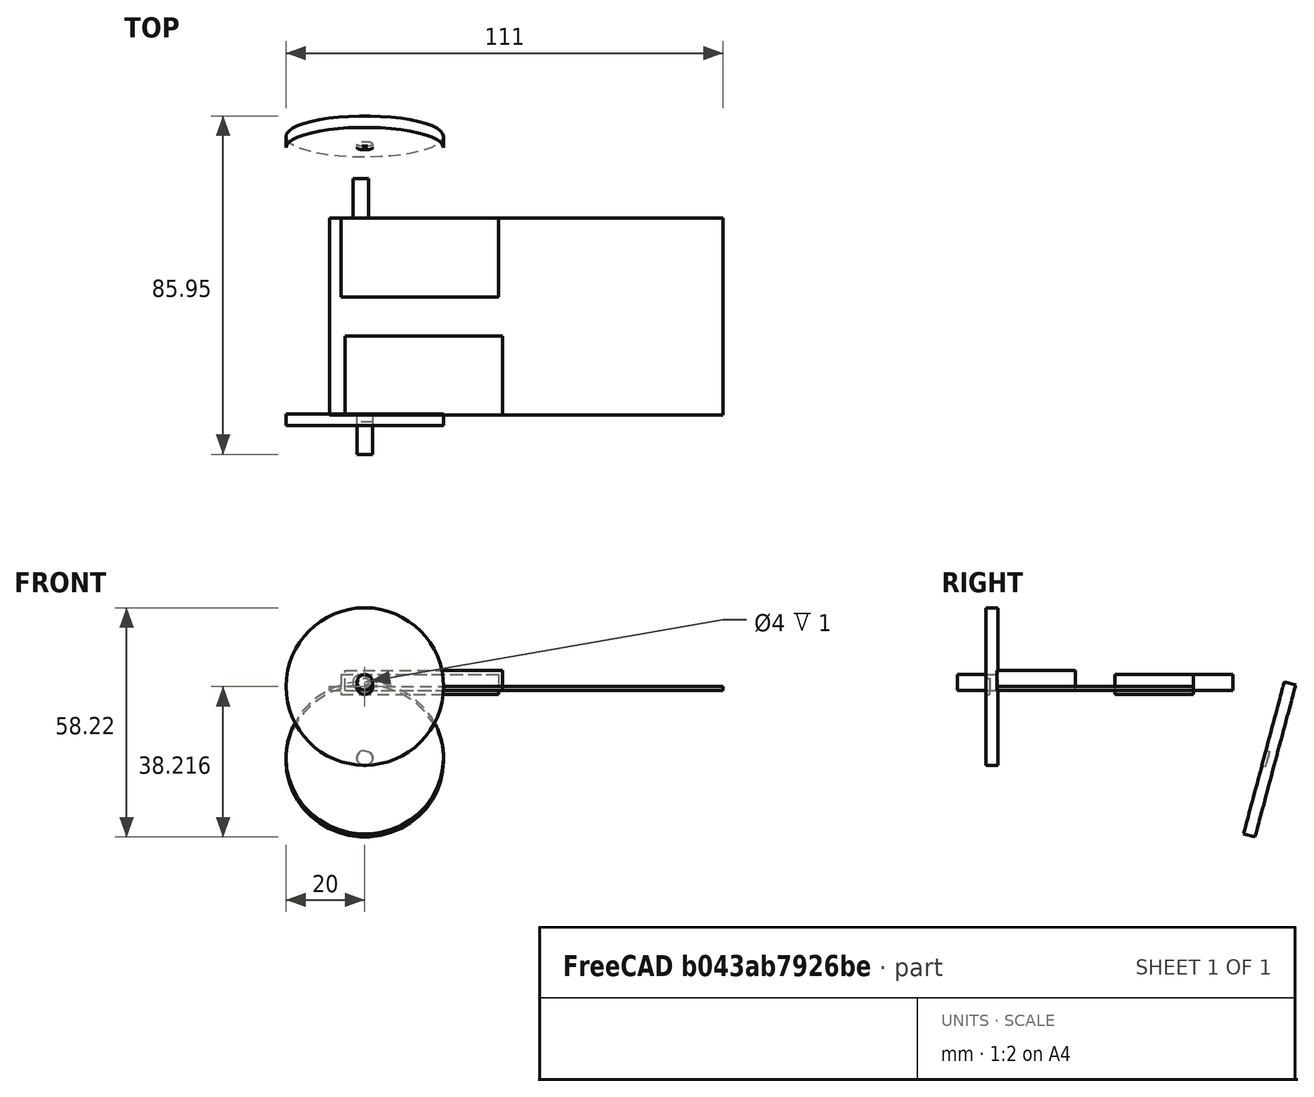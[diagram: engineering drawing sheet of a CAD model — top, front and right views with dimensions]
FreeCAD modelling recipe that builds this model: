
FCSTD DOCUMENT  (FreeCAD 1.0R38806 (Git))
Label: cutrebot
License: All rights reserved
LicenseURL: https://en.wikipedia.org/wiki/All_rights_reserved
objects: Part::Cylinder×6, Part::Box×3, Part::MultiFuse×2, Part::Cut×2
note: 13 computed .brp shape members not serialized (recipe doc carries the construction recipe); baked Part::Feature solids carry a one-line shape summary decoded from their .brp

FEATURE [Part::Box] Box  label="Cube"
  AttacherType = Attacher::AttachEngine3D
  Height = 5
  Length = 40
  Width = 20
FEATURE [Part::Cylinder] Cylinder
  Angle = 360
  AttacherType = Attacher::AttachEngine3D
  FirstAngle = 0
  Height = 10
  Placement = pos=(5,4e-16,2) rot=(1,0,0;1.5708rad)
  Radius = 2
  SecondAngle = 0
FEATURE [Part::MultiFuse] Fusion  label="Servo-con-eje"
  Placement = pos=(3,50,4) rot=(1,0,0;3.14159rad)
  Shapes = -> [Box,Cylinder]
FEATURE [Part::Box] Box001  label="Cube001"
  AttacherType = Attacher::AttachEngine3D
  Height = 1
  Length = 100
  Width = 50
FEATURE [Part::Cylinder] Cylinder001
  Angle = 360
  AttacherType = Attacher::AttachEngine3D
  FirstAngle = 0
  Height = 3
  Placement = pos=(73,0,0) rot=(0,0,1;0rad)
  Radius = 20
  SecondAngle = 0
FEATURE [Part::Cylinder] Cylinder002
  Angle = 360
  AttacherType = Attacher::AttachEngine3D
  FirstAngle = 0
  Height = 10
  Placement = pos=(73,4e-16,2) rot=(0,0,1;0rad)
  Radius = 2
  SecondAngle = 0
FEATURE [Part::Cut] Cut
  Base = -> Cylinder001
  Placement = pos=(-64,0.258819,0.965926) rot=(1,0,0;1.5708rad)
  Tool = -> Cylinder002
FEATURE [Part::Box] Box002  label="Cube002"
  AttacherType = Attacher::AttachEngine3D
  Height = 5
  Length = 40
  Width = 20
FEATURE [Part::Cylinder] Cylinder003
  Angle = 360
  AttacherType = Attacher::AttachEngine3D
  FirstAngle = 0
  Height = 10
  Placement = pos=(5,4e-16,2) rot=(1,0,0;1.5708rad)
  Radius = 2
  SecondAngle = 0
FEATURE [Part::MultiFuse] Fusion001  label="Servo-con-eje001"
  Placement = pos=(4,0,0) rot=(0,0,1;0rad)
  Shapes = -> [Box002,Cylinder003]
FEATURE [Part::Cylinder] Cylinder004
  Angle = 360
  AttacherType = Attacher::AttachEngine3D
  FirstAngle = 0
  Height = 3
  Placement = pos=(73,0,0) rot=(0,0,1;0rad)
  Radius = 20
  SecondAngle = 0
FEATURE [Part::Cylinder] Cylinder005
  Angle = 360
  AttacherType = Attacher::AttachEngine3D
  FirstAngle = 0
  Height = 10
  Placement = pos=(73,4e-16,2) rot=(0,0,1;0rad)
  Radius = 2
  SecondAngle = 0
FEATURE [Part::Cut] Cut001
  Base = -> Cylinder004
  Placement = pos=(-64,70.7714,-17.9279) rot=(1,0,0;1.309rad)
  Tool = -> Cylinder005
